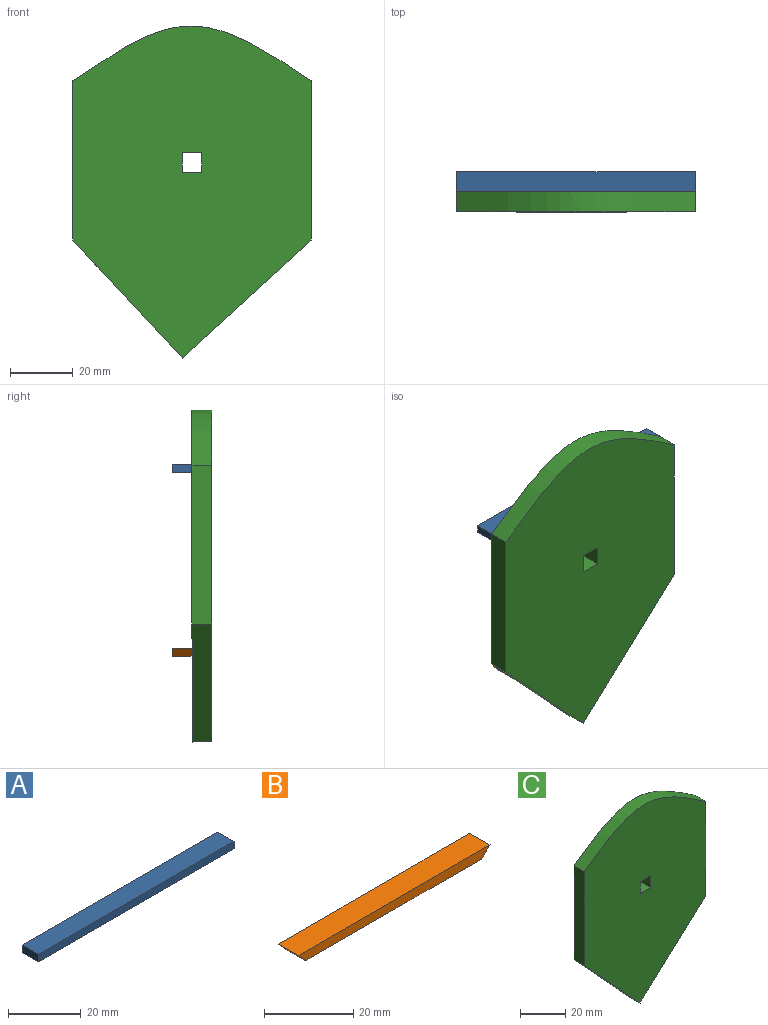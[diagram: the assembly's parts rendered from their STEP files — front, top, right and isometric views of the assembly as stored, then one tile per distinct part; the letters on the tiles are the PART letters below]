
ASSEMBLY  parts=3 mates=2
PART A: 6 faces, bbox 76.2x6.4x2.5 mm
  f0: plane 6.35x2.54mm, normal (-1,0,0), area 16.1mm2, adj f1,f3,f4,f5
  f1: plane 76.2x6.35mm, normal (0,0,-1), area 483.9mm2, adj f0,f2,f4,f5
  f2: plane 6.35x2.54mm, normal (1,0,0), area 16.1mm2, adj f1,f3,f4,f5
  f3: plane 76.2x6.35mm, normal (0,0,1), area 483.9mm2, adj f0,f2,f4,f5
  f4: plane 76.2x2.54mm, normal (0,-1,0), area 193.5mm2, adj f0,f1,f2,f3
  f5: plane 76.2x2.54mm, normal (0,1,0), area 193.5mm2, adj f0,f1,f2,f3
PART B: 6 faces, bbox 60.8x6.4x2.5 mm
  f0: plane 60.81x6.35mm, normal (0,0,1), area 386.2mm2, adj f1,f3,f4,f5
  f1: plane 6.35x2.54mm, normal (-0.73,0,-0.68), area 22mm2, adj f0,f2,f4,f5
  f2: plane 55.69x6.35mm, normal (0,0,-1), area 353.6mm2, adj f1,f3,f4,f5
  f3: plane 6.35x2.78mm, normal (0.67,0,-0.74), area 23.9mm2, adj f0,f2,f4,f5
  f4: plane 60.81x2.54mm, normal (0,-1,0), area 148mm2, adj f0,f1,f2,f3
  f5: plane 60.81x2.54mm, normal (0,1,0), area 148mm2, adj f0,f1,f2,f3
PART C: 11 faces, bbox 76.2x6.4x107.1 mm
  f0: plane 6.35x6.35mm, normal (1,0,0), area 40.3mm2, adj f1,f8,f9,f10
  f1: plane 6.35x6.35mm, normal (0,0,-1), area 40.3mm2, adj f0,f2,f9,f10
  f2: plane 6.35x6.35mm, normal (-1,0,0), area 40.3mm2, adj f1,f8,f9,f10
  f3: plane 37.74x34.93mm, normal (-0.73,0,-0.68), area 326.5mm2, adj f4,f7,f9,f10
  f4: plane 41.28x37.74mm, normal (0.67,0,-0.74), area 355.1mm2, adj f3,f5,f9,f10
  f5: plane 50.8x6.35mm, normal (1,0,0), area 322.6mm2, adj f4,f6,f9,f10
  f6: extruded ~76.2x17.64mm, area 541.3mm2, adj f5,f7,f9,f10
  f7: plane 50.8x6.35mm, normal (-1,0,0), area 322.6mm2, adj f3,f6,f9,f10
  f8: plane 6.35x6.35mm, normal (0,0,1), area 40.3mm2, adj f0,f2,f9,f10
  f9: plane 107.11x76.2mm, normal (0,-1,0), area 6108.8mm2, adj f0,f1,f2,f3,f4,f5,f6,f7
  f10: plane 107.11x76.2mm, normal (0,1,0), area 6108.8mm2, adj f0,f1,f2,f3,f4,f5,f6,f7
PLACE A t=(-94.04,41.9,12.75)mm
PLACE B t=(-271.31,41.9,-106.63)mm
PLACE C t=(-115.06,35.55,-28.68)mm
MATE fastened B.f4 <-> C.f10  axis (0,-1,0) through (-132.9,35.55,-41.06)mm
MATE fastened A.f4 <-> C.f10  axis (0,-1,0) through (-132.14,35.55,17.62)mm
